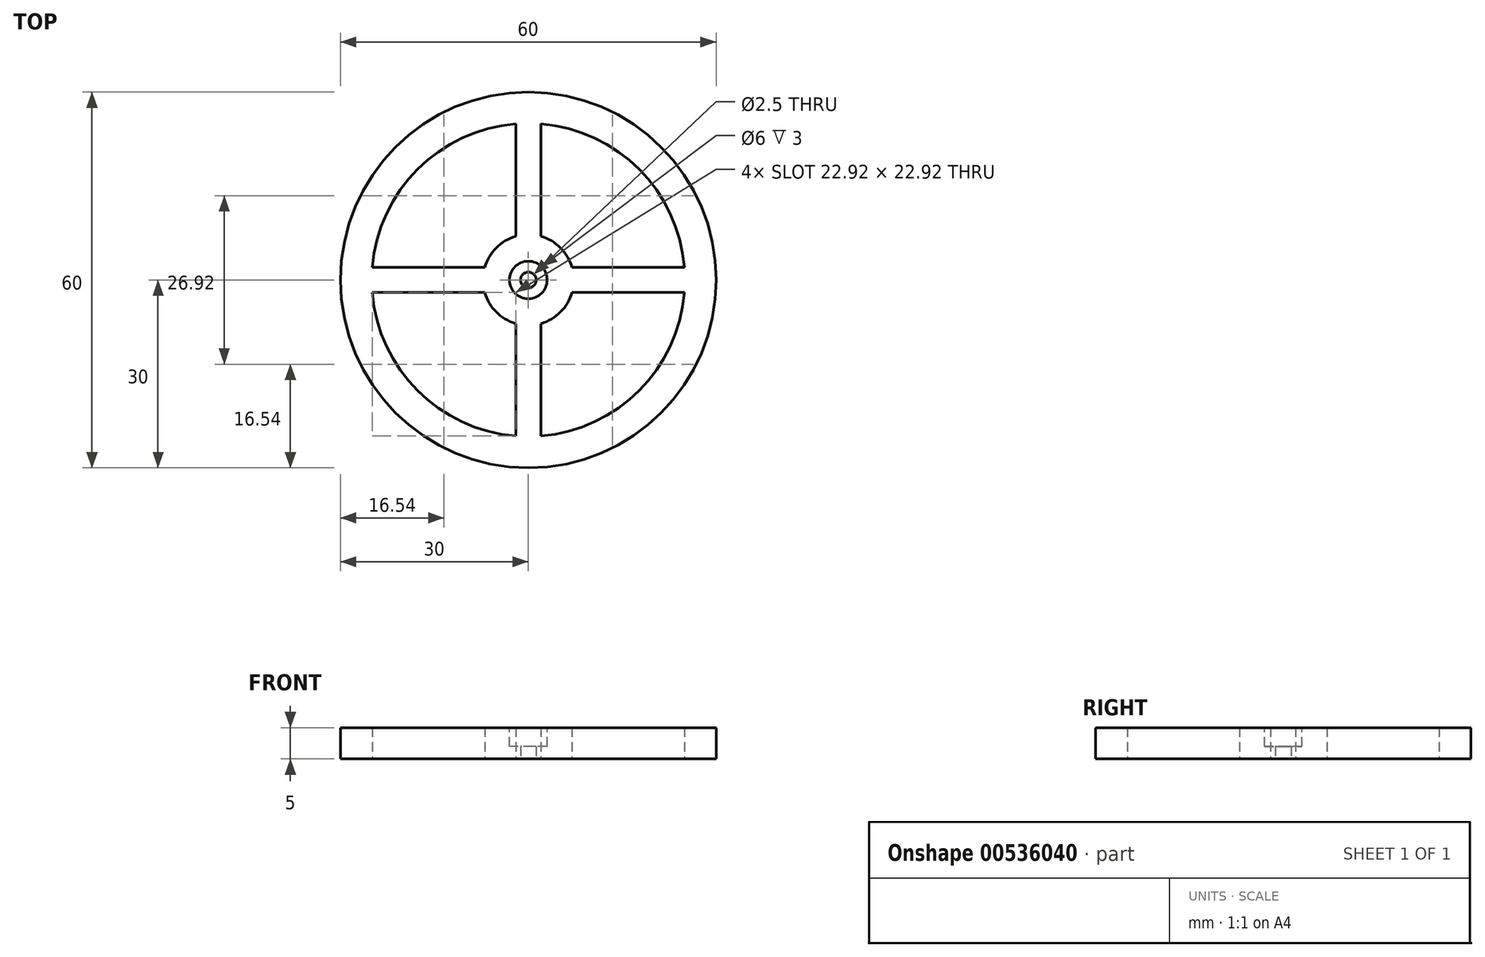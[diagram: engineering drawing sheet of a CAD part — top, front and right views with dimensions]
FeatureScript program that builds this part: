
annotation { "Feature Type Name" : "Feature", "Feature Type Description" : "" }
export const myFeature = defineFeature(function(context is Context, id is Id, definition is map)
    precondition{}
    {
        {
            var Q0;
            Q0=qCreatedBy(makeId("Top.planeOp"),FACE);
            var sketch = newSketch(context, id + "F0", { "sketchPlane" : qUnion([Q0])});
            skCircle(sketch, "E0", {"center": v(0, 0) * mm, "radius": 30 * mm});
            skArc(sketch, "E1", {"start": v(-2, 24.92) * mm, "mid": v(-17.68, 17.68) * mm, "end": v(-24.92, 2) * mm});
            skCircle(sketch, "E2", {"center": v(0, 0) * mm, "radius": 1.25 * mm});
            skArc(sketch, "E3", {"start": v(2, -6.97) * mm, "mid": v(5.13, -5.13) * mm, "end": v(6.97, -2) * mm});
            skLineSegment(sketch, "E4", {"start": v(-2, 24.92) * mm, "end": v(-2, 6.97) * mm});
            skLineSegment(sketch, "E5", {"start": v(2, -24.92) * mm, "end": v(2, -6.97) * mm});
            skArc(sketch, "E6.trimOffspring", {"start": v(2, -24.92) * mm, "mid": v(17.68, -17.68) * mm, "end": v(24.92, -2) * mm});
            skArc(sketch, "E7.trimOffspring", {"start": v(-2, 6.97) * mm, "mid": v(-5.13, 5.13) * mm, "end": v(-6.97, 2) * mm});
            skLineSegment(sketch, "E8.trimOffspring", {"start": v(-2, -6.97) * mm, "end": v(-2, -24.92) * mm});
            skLineSegment(sketch, "E9.trimOffspring", {"start": v(2, 6.97) * mm, "end": v(2, 24.92) * mm});
            skLineSegment(sketch, "E10", {"start": v(-24.92, 2) * mm, "end": v(-6.97, 2) * mm});
            skLineSegment(sketch, "E11", {"start": v(-24.92, -2) * mm, "end": v(-6.97, -2) * mm});
            skPoint(sketch, "E12.orphan", {"position": v(-19.32, 2) * mm});
            skPoint(sketch, "E13.orphan", {"position": v(-19.32, -2) * mm});
            skArc(sketch, "E14.trimOffspring", {"start": v(24.92, 2) * mm, "mid": v(17.68, 17.68) * mm, "end": v(2, 24.92) * mm});
            skArc(sketch, "E15.trimOffspring", {"start": v(6.97, 2) * mm, "mid": v(5.13, 5.13) * mm, "end": v(2, 6.97) * mm});
            skArc(sketch, "E16.trimOffspring", {"start": v(-24.92, -2) * mm, "mid": v(-17.68, -17.68) * mm, "end": v(-2, -24.92) * mm});
            skArc(sketch, "E17.trimOffspring", {"start": v(-6.97, -2) * mm, "mid": v(-5.13, -5.13) * mm, "end": v(-2, -6.97) * mm});
            skLineSegment(sketch, "E18.trimOffspring", {"start": v(6.97, 2) * mm, "end": v(24.92, 2) * mm});
            skLineSegment(sketch, "E19.trimOffspring", {"start": v(6.97, -2) * mm, "end": v(24.92, -2) * mm});
            skSolve(sketch);
        }
        {
            var Q0;
            Q0 = qSketchRegion(id + "F0", true);
            extrude(context, id + "F1", {"entities" : qUnion([Q0]), "depth" : 5 * mm, "offsetDistance" : 25 * mm});
        }
        {
            var Q0;
            Q0=makeQuery(id+"F1.opExtrude","CAP_FACE",FACE,{"disambiguationData":[OSD([sQuery(id+"F0.wireOp",EDGE,"E0"),sQuery(id+"F0.wireOp",EDGE,"E1"),sQuery(id+"F0.wireOp",EDGE,"E2"),sQuery(id+"F0.wireOp",EDGE,"E3"),sQuery(id+"F0.wireOp",EDGE,"E4"),sQuery(id+"F0.wireOp",EDGE,"E5"),sQuery(id+"F0.wireOp",EDGE,"E6.trimOffspring"),sQuery(id+"F0.wireOp",EDGE,"E7.trimOffspring"),sQuery(id+"F0.wireOp",EDGE,"E8.trimOffspring"),sQuery(id+"F0.wireOp",EDGE,"E9.trimOffspring"),sQuery(id+"F0.wireOp",EDGE,"E10"),sQuery(id+"F0.wireOp",EDGE,"E11"),sQuery(id+"F0.wireOp",EDGE,"E14.trimOffspring"),sQuery(id+"F0.wireOp",EDGE,"E15.trimOffspring"),sQuery(id+"F0.wireOp",EDGE,"E16.trimOffspring"),sQuery(id+"F0.wireOp",EDGE,"E17.trimOffspring"),sQuery(id+"F0.wireOp",EDGE,"E18.trimOffspring"),sQuery(id+"F0.wireOp",EDGE,"E19.trimOffspring")])],"isStart":false});
            var sketch = newSketch(context, id + "F2", { "sketchPlane" : qUnion([Q0])});
            skCircle(sketch, "E20", {"center": v(0, 0) * mm, "radius": 3 * mm});
            skSolve(sketch);
        }
        {
            var Q0;
            Q0=makeQuery(id+"F2.imprint","IMPRINT",FACE,{"disambiguationData":[TD([[makeQuery(id+"F2.imprint","IMPRINT",EDGE,{"derivedFrom":sQuery(id+"F2.wireOp",EDGE,"E20")}),1.0]])]});
            extrude(context, id + "F3", {"entities" : qUnion([Q0]), "operationType" : NewBodyOperationType.REMOVE, "oppositeDirection" : true, "depth" : 3 * mm, "offsetDistance" : 25 * mm});
        }
    });
